# Revit family: Drain_Trap_Drum-Zurn-Z450B
name_source: partatom
category: Plumbing Fixtures
units: mm (PartAtom-declared; Revit-internal decimal feet)

## family parameters
Always vertical = Yes
Cut with Voids When Loaded = No
Maintain Annotation Orientation = No
OmniClass Number = 23.45.55.21
OmniClass Title = Drains (Wastes)
Part Type = Normal
Room Calculation Point = No
Round Connector Dimension = Use Radius
Shared = No
Work Plane-Based = No

## types (52) — shared parameters
Assembly Code = D2030300
CW Connection = No
Default Elevation = 20 "
Description = DRUM TRAP DRAIN WITH TYPE B STRAINER
HW Connection = No
Main Material = Iron - Zurn - Cast - Painted - Blue
Manufacturer = Zurn Water, LLC
Manufacurer Brand = Zurn
Modified Date = 12/26/2025
Product Documentation Link = https://files.zurn.com
Product Page URL = https://www.zurn.com
Product data url = https://www.bimobject.com
URL = www.zurn.com
Vent Connection = No
WFU = 1
Waste Connection = Yes
zero-valued in all types: CWFU, HWFU

## per-type parameters (varying)
| type | Approx. Wt. Lbs. | Body Height_E | Body Outer Radius | Connector Radius | Dim H | Dim M | Grate Material | Grate Open Area | Grate Radius | Model | Pipe Size_A Inside Diameter | Pipe Size_A Nominal Diameter | Pipe Size_A Outer Diameter | Strainer Diameter (B) | Type Comments |
| ZN450B-2IP-5 | 18.00 lbf | 6.531 " | 4.5 " | 1 " | 6.063 " | 1.469 " | Bronze - Zurn - Polished Nickel | 8 in² | 2.325 " | ZN450B | 2.067 " | 2 " | 2.375 " | 5 " | ZN450B with 5 Inch Strainer and 2 Inch Threaded Side Outlet |
| ZN450B-3IP-5 | 18.00 lbf | 6.531 " | 4.5 " | 1.5 " | 6.438 " | 2.094 " | Bronze - Zurn - Polished Nickel | 8 in² | 2.325 " | ZN450B | 3.068 " | 3 " | 3.5 " | 5 " | ZN450B with 5 Inch Strainer and 3 Inch Threaded Side Outlet |
| ZN450B-4IP-5 | 18.00 lbf | 7.438 " | 5 " | 2 " | 6.875 " | 2.594 " | Bronze - Zurn - Polished Nickel | 8 in² | 2.325 " | ZN450B | 4.028 " | 4 " | 4.5 " | 5 " | ZN450B with 5 Inch Strainer and 4 Inch Threaded Side Outlet |
| ZN450B-2NH-5 | 18.00 lbf | 7.438 " | 5 " | 1 " | 11 " | 2 " | Bronze - Zurn - Polished Nickel | 8 in² | 2.325 " | ZN450B | 2.067 " | 2 " | 2.375 " | 5 " | ZN450B with 5 Inch Strainer and 2 Inch No-Hub Side Outlet |
| ZN450B-3NH-5 | 18.00 lbf | 7.438 " | 5 " | 1.5 " | 11 " | 2.563 " | Bronze - Zurn - Polished Nickel | 8 in² | 2.325 " | ZN450B | 3.068 " | 3 " | 3.5 " | 5 " | ZN450B with 5 Inch Strainer and 3 Inch No-Hub Side Outlet |
| ZN450B-4NH-5 | 18.00 lbf | 7.438 " | 5 " | 2 " | 11 " | 2.594 " | Bronze - Zurn - Polished Nickel | 8 in² | 2.325 " | ZN450B | 4.028 " | 4 " | 4.5 " | 5 " | ZN450B with 5 Inch Strainer and 4 Inch No-Hub Side Outlet |
| ZN450B-2IP-6 | 19.00 lbf | 6.531 " | 4.5 " | 1 " | 6.063 " | 1.469 " | Bronze - Zurn - Polished Nickel | 9 in² | 2.825 " | ZN450B | 2.067 " | 2 " | 2.375 " | 6 " | ZN450B with 6 Inch Strainer and 2 Inch Threaded Side Outlet |
| ZN450B-3IP-6 | 19.00 lbf | 6.531 " | 4.5 " | 1.5 " | 6.438 " | 2.094 " | Bronze - Zurn - Polished Nickel | 9 in² | 2.825 " | ZN450B | 3.068 " | 3 " | 3.5 " | 6 " | ZN450B with 6 Inch Strainer and 3 Inch Threaded Side Outlet |
| ZN450B-4IP-6 | 19.00 lbf | 7.438 " | 5 " | 2 " | 6.875 " | 2.594 " | Bronze - Zurn - Polished Nickel | 9 in² | 2.825 " | ZN450B | 4.028 " | 4 " | 4.5 " | 6 " | ZN450B with 6 Inch Strainer and 4 Inch Threaded Side Outlet |
| ZN450B-2NH-6 | 19.00 lbf | 7.438 " | 5 " | 1 " | 11 " | 2 " | Bronze - Zurn - Polished Nickel | 9 in² | 2.825 " | ZN450B | 2.067 " | 2 " | 2.375 " | 6 " | ZN450B with 6 Inch Strainer and 2 Inch No-Hub Side Outlet |
| ZN450B-3NH-6 | 19.00 lbf | 7.438 " | 5 " | 1.5 " | 11 " | 2.563 " | Bronze - Zurn - Polished Nickel | 9 in² | 2.825 " | ZN450B | 3.068 " | 3 " | 3.5 " | 6 " | ZN450B with 6 Inch Strainer and 3 Inch No-Hub Side Outlet |
| ZN450B-4NH-6 | 19.00 lbf | 7.438 " | 5 " | 2 " | 11 " | 2.594 " | Bronze - Zurn - Polished Nickel | 9 in² | 2.825 " | ZN450B | 4.028 " | 4 " | 4.5 " | 6 " | ZN450B with 6 Inch Strainer and 4 Inch No-Hub Side Outlet |
| ZN450B-2IP-7 | 33.00 lbf | 6.531 " | 4.5 " | 1 " | 6.063 " | 1.469 " | Bronze - Zurn - Polished Nickel | 12 in² | 3.325 " | ZN450B | 2.067 " | 2 " | 2.375 " | 7 " | ZN450B with 7 Inch Strainer and 2 Inch Threaded Side Outlet |
| ZN450B-3IP-7 | 33.00 lbf | 6.531 " | 4.5 " | 1.5 " | 6.438 " | 2.094 " | Bronze - Zurn - Polished Nickel | 12 in² | 3.325 " | ZN450B | 3.068 " | 3 " | 3.5 " | 7 " | ZN450B with 7 Inch Strainer and 3 Inch Threaded Side Outlet |
| ZN450B-4IP-7 | 33.00 lbf | 7.438 " | 5 " | 2 " | 6.875 " | 2.594 " | Bronze - Zurn - Polished Nickel | 12 in² | 3.325 " | ZN450B | 4.028 " | 4 " | 4.5 " | 7 " | ZN450B with 7 Inch Strainer and 4 Inch Threaded Side Outlet |
| ZN450B-2NH-7 | 33.00 lbf | 7.438 " | 5 " | 1 " | 11 " | 2 " | Bronze - Zurn - Polished Nickel | 12 in² | 3.325 " | ZN450B | 2.067 " | 2 " | 2.375 " | 7 " | ZN450B with 7 Inch Strainer and 2 Inch No-Hub Side Outlet |
| ZN450B-3NH-7 | 33.00 lbf | 7.438 " | 5 " | 1.5 " | 11 " | 2.563 " | Bronze - Zurn - Polished Nickel | 12 in² | 3.325 " | ZN450B | 3.068 " | 3 " | 3.5 " | 7 " | ZN450B with 7 Inch Strainer and 3 Inch No-Hub Side Outlet |
| ZN450B-4NH-7 | 33.00 lbf | 7.438 " | 5 " | 2 " | 11 " | 2.594 " | Bronze - Zurn - Polished Nickel | 12 in² | 3.325 " | ZN450B | 4.028 " | 4 " | 4.5 " | 7 " | ZN450B with 7 Inch Strainer and 4 Inch No-Hub Side Outlet |
| ZN450B-2IP-8 | 16.00 lbf | 6.531 " | 4.5 " | 1 " | 6.063 " | 1.469 " | Bronze - Zurn - Polished Nickel | 18 in² | 3.825 " | ZN450B | 2.067 " | 2 " | 2.375 " | 8 " | ZN450B with 8 Inch Strainer and 2 Inch Threaded Side Outlet |
| ZN450B-3IP-8 | 16.00 lbf | 6.531 " | 4.5 " | 1.5 " | 6.438 " | 2.094 " | Bronze - Zurn - Polished Nickel | 18 in² | 3.825 " | ZN450B | 3.068 " | 3 " | 3.5 " | 8 " | ZN450B with 8 Inch Strainer and 3 Inch Threaded Side Outlet |
| ZN450B-4IP-8 | 16.00 lbf | 7.438 " | 5 " | 2 " | 6.875 " | 2.594 " | Bronze - Zurn - Polished Nickel | 18 in² | 3.825 " | ZN450B | 4.028 " | 4 " | 4.5 " | 8 " | ZN450B with 8 Inch Strainer and 4 Inch Threaded Side Outlet |
| ZN450B-2NH-8 | 16.00 lbf | 7.438 " | 5 " | 1 " | 11 " | 2 " | Bronze - Zurn - Polished Nickel | 18 in² | 3.825 " | ZN450B | 2.067 " | 2 " | 2.375 " | 8 " | ZN450B with 8 Inch Strainer and 2 Inch No-Hub Side Outlet |
| ZN450B-3NH-8 | 16.00 lbf | 7.438 " | 5 " | 1.5 " | 11 " | 2.563 " | Bronze - Zurn - Polished Nickel | 18 in² | 3.825 " | ZN450B | 3.068 " | 3 " | 3.5 " | 8 " | ZN450B with 8 Inch Strainer and 3 Inch No-Hub Side Outlet |
| ZN450B-4NH-8 | 16.00 lbf | 7.438 " | 5 " | 2 " | 11 " | 2.594 " | Bronze - Zurn - Polished Nickel | 18 in² | 3.825 " | ZN450B | 4.028 " | 4 " | 4.5 " | 8 " | ZN450B with 8 Inch Strainer and 4 Inch No-Hub Side Outlet |
| ZN450B-4IP-10 | 33.00 lbf | 7.438 " | 5 " | 2 " | 6.875 " | 2.594 " | Bronze - Zurn - Polished Nickel | 26 in² | 4.825 " | ZN450B | 4.028 " | 4 " | 4.5 " | 10 " | ZN450B with 10 Inch Strainer and 4 Inch Threaded Side Outlet |
| ZN450B-4NH-10 | 33.00 lbf | 7.438 " | 5 " | 2 " | 11 " | 2.594 " | Bronze - Zurn - Polished Nickel | 26 in² | 4.825 " | ZN450B | 4.028 " | 4 " | 4.5 " | 10 " | ZN450B with 10 Inch Strainer and 4 Inch No-Hub Side Outlet |
| ZB450B-2IP-5 | 18.00 lbf | 7.438 " | 4.5 " | 1 " | 6.063 " | 1.469 " | Bronze - Zurn - Polished | 8 in² | 2.325 " | ZB450B | 2.067 " | 2 " | 2.375 " | 5 " | ZB450B with 5 Inch Strainer and 2 Inch Threaded Side Outlet |
| ZB450B-3IP-5 | 18.00 lbf | 6.531 " | 4.5 " | 1.5 " | 6.438 " | 2.094 " | Bronze - Zurn - Polished | 8 in² | 2.325 " | ZB450B | 3.068 " | 3 " | 3.5 " | 5 " | ZB450B with 5 Inch Strainer and 3 Inch Threaded Side Outlet |
| ZB450B-4IP-5 | 18.00 lbf | 7.438 " | 5 " | 2 " | 6.875 " | 2.594 " | Bronze - Zurn - Polished | 8 in² | 2.325 " | ZB450B | 4.028 " | 4 " | 4.5 " | 5 " | ZB450B with 5 Inch Strainer and 4 Inch Threaded Side Outlet |
| ZB450B-2NH-5 | 18.00 lbf | 7.438 " | 5 " | 1 " | 11 " | 2 " | Bronze - Zurn - Polished | 8 in² | 2.325 " | ZB450B | 2.067 " | 2 " | 2.375 " | 5 " | ZB450B with 5 Inch Strainer and 2 Inch No-Hub Side Outlet |
| ZB450B-3NH-5 | 18.00 lbf | 7.438 " | 5 " | 1.5 " | 11 " | 2.563 " | Bronze - Zurn - Polished | 8 in² | 2.325 " | ZB450B | 3.068 " | 3 " | 3.5 " | 5 " | ZB450B with 5 Inch Strainer and 3 Inch No-Hub Side Outlet |
| ZB450B-4NH-5 | 18.00 lbf | 7.438 " | 5 " | 2 " | 11 " | 2.594 " | Bronze - Zurn - Polished | 8 in² | 2.325 " | ZB450B | 4.028 " | 4 " | 4.5 " | 5 " | ZB450B with 5 Inch Strainer and 4 Inch No-Hub Side Outlet |
| ZB450B-2IP-6 | 19.00 lbf | 6.531 " | 4.5 " | 1 " | 6.063 " | 1.469 " | Bronze - Zurn - Polished | 9 in² | 2.825 " | ZB450B | 2.067 " | 2 " | 2.375 " | 6 " | ZB450B with 6 Inch Strainer and 2 Inch Threaded Side Outlet |
| ZB450B-3IP-6 | 19.00 lbf | 6.531 " | 4.5 " | 1.5 " | 6.438 " | 2.094 " | Bronze - Zurn - Polished | 9 in² | 2.825 " | ZB450B | 3.068 " | 3 " | 3.5 " | 6 " | ZB450B with 6 Inch Strainer and 3 Inch Threaded Side Outlet |
| ZB450B-4IP-6 | 19.00 lbf | 7.438 " | 5 " | 2 " | 6.875 " | 2.594 " | Bronze - Zurn - Polished | 9 in² | 2.825 " | ZB450B | 4.028 " | 4 " | 4.5 " | 6 " | ZB450B with 6 Inch Strainer and 4 Inch Threaded Side Outlet |
| ZB450B-2NH-6 | 19.00 lbf | 7.438 " | 5 " | 1 " | 11 " | 2 " | Bronze - Zurn - Polished | 9 in² | 2.825 " | ZB450B | 2.067 " | 2 " | 2.375 " | 6 " | ZB450B with 6 Inch Strainer and 2 Inch No-Hub Side Outlet |
| ZB450B-3NH-6 | 19.00 lbf | 7.438 " | 5 " | 1.5 " | 11 " | 2.563 " | Bronze - Zurn - Polished | 9 in² | 2.825 " | ZB450B | 3.068 " | 3 " | 3.5 " | 6 " | ZB450B with 6 Inch Strainer and 3 Inch No-Hub Side Outlet |
| ZB450B-4NH-6 | 19.00 lbf | 7.438 " | 5 " | 2 " | 11 " | 2.594 " | Bronze - Zurn - Polished | 9 in² | 2.825 " | ZB450B | 4.028 " | 4 " | 4.5 " | 6 " | ZB450B with 6 Inch Strainer and 4 Inch No-Hub Side Outlet |
| ZB450B-2IP-7 | 33.00 lbf | 6.531 " | 4.5 " | 1 " | 6.063 " | 1.469 " | Bronze - Zurn - Polished | 12 in² | 3.325 " | ZB450B | 2.067 " | 2 " | 2.375 " | 7 " | ZB450B with 7 Inch Strainer and 2 Inch Threaded Side Outlet |
| ZB450B-3IP-7 | 33.00 lbf | 6.531 " | 4.5 " | 1.5 " | 6.438 " | 2.094 " | Bronze - Zurn - Polished | 12 in² | 3.325 " | ZB450B | 3.068 " | 3 " | 3.5 " | 7 " | ZB450B with 7 Inch Strainer and 3 Inch Threaded Side Outlet |
| ZB450B-4IP-7 | 33.00 lbf | 7.438 " | 5 " | 2 " | 6.875 " | 2.594 " | Bronze - Zurn - Polished | 12 in² | 3.325 " | ZB450B | 4.028 " | 4 " | 4.5 " | 7 " | ZB450B with 7 Inch Strainer and 4 Inch Threaded Side Outlet |
| ZB450B-2NH-7 | 33.00 lbf | 7.438 " | 5 " | 1 " | 11 " | 2 " | Bronze - Zurn - Polished | 12 in² | 3.325 " | ZB450B | 2.067 " | 2 " | 2.375 " | 7 " | ZB450B with 7 Inch Strainer and 2 Inch No-Hub Side Outlet |
| ZB450B-3NH-7 | 33.00 lbf | 7.438 " | 5 " | 1.5 " | 11 " | 2.563 " | Bronze - Zurn - Polished | 12 in² | 3.325 " | ZB450B | 3.068 " | 3 " | 3.5 " | 7 " | ZB450B with 7 Inch Strainer and 3 Inch No-Hub Side Outlet |
| ZB450B-4NH-7 | 33.00 lbf | 7.438 " | 5 " | 2 " | 11 " | 2.594 " | Bronze - Zurn - Polished | 12 in² | 3.325 " | ZB450B | 4.028 " | 4 " | 4.5 " | 7 " | ZB450B with 7 Inch Strainer and 4 Inch No-Hub Side Outlet |
| ZB450B-2IP-8 | 16.00 lbf | 6.531 " | 4.5 " | 1 " | 6.063 " | 1.469 " | Bronze - Zurn - Polished | 18 in² | 3.825 " | ZB450B | 2.067 " | 2 " | 2.375 " | 8 " | ZB450B with 8 Inch Strainer and 2 Inch Threaded Side Outlet |
| ZB450B-3IP-8 | 16.00 lbf | 6.531 " | 4.5 " | 1.5 " | 6.438 " | 2.094 " | Bronze - Zurn - Polished | 18 in² | 3.825 " | ZB450B | 3.068 " | 3 " | 3.5 " | 8 " | ZB450B with 8 Inch Strainer and 3 Inch Threaded Side Outlet |
| ZB450B-4IP-8 | 16.00 lbf | 7.438 " | 5 " | 2 " | 6.875 " | 2.594 " | Bronze - Zurn - Polished | 18 in² | 3.825 " | ZB450B | 4.028 " | 4 " | 4.5 " | 8 " | ZB450B with 8 Inch Strainer and 4 Inch Threaded Side Outlet |
| ZB450B-2NH-8 | 16.00 lbf | 7.438 " | 5 " | 1 " | 11 " | 2 " | Bronze - Zurn - Polished | 18 in² | 3.825 " | ZB450B | 2.067 " | 2 " | 2.375 " | 8 " | ZB450B with 8 Inch Strainer and 2 Inch No-Hub Side Outlet |
| ZB450B-3NH-8 | 16.00 lbf | 7.438 " | 5 " | 1.5 " | 11 " | 2.563 " | Bronze - Zurn - Polished | 18 in² | 3.825 " | ZB450B | 3.068 " | 3 " | 3.5 " | 8 " | ZB450B with 8 Inch Strainer and 3 Inch No-Hub Side Outlet |
| ZB450B-4NH-8 | 16.00 lbf | 7.438 " | 5 " | 2 " | 11 " | 2.594 " | Bronze - Zurn - Polished | 18 in² | 3.825 " | ZB450B | 4.028 " | 4 " | 4.5 " | 8 " | ZB450B with 8 Inch Strainer and 4 Inch No-Hub Side Outlet |
| ZB450B-4IP-10 | 33.00 lbf | 7.438 " | 5 " | 2 " | 6.875 " | 2.594 " | Bronze - Zurn - Polished | 26 in² | 4.825 " | ZB450B | 4.028 " | 4 " | 4.5 " | 10 " | ZB450B with 10 Inch Strainer and 4 Inch Threaded Side Outlet |
| ZB450B-4NH-10 | 33.00 lbf | 7.438 " | 5 " | 2 " | 11 " | 2.594 " | Bronze - Zurn - Polished | 26 in² | 4.825 " | ZB450B | 4.028 " | 4 " | 4.5 " | 10 " | ZB450B with 10 Inch Strainer and 4 Inch No-Hub Side Outlet |

## geometry (parser evidence)
native form markers: Sweep x4
no freeform markers — native parametric forms only
